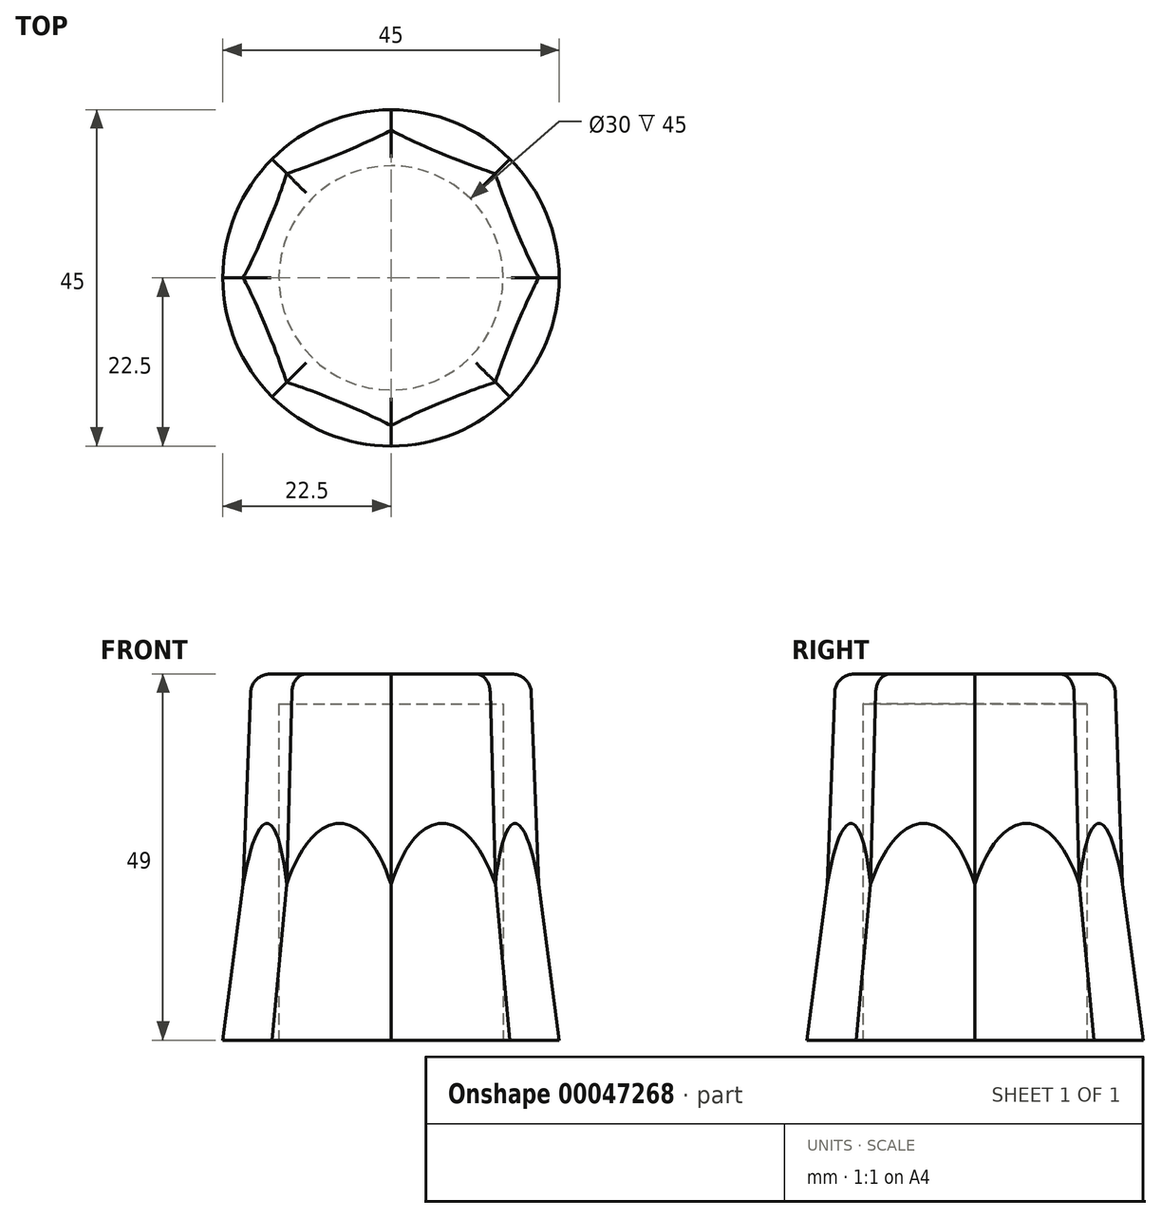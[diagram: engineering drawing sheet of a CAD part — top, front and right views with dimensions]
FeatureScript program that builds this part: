
annotation { "Feature Type Name" : "Feature", "Feature Type Description" : "" }
export const myFeature = defineFeature(function(context is Context, id is Id, definition is map)
    precondition{}
    {
        {
            assignVariable(context, id + "F0", {"name" : "thickness", "anyValue" : 4 * mm});
        }
        {
            var Q0;
            Q0=qCreatedBy(makeId("Top.planeOp"),FACE);
            var sketch = newSketch(context, id + "F1", { "sketchPlane" : qUnion([Q0])});
            skCircle(sketch, "E0.cCircle", {"center": v(0, 0) * mm, "radius": 19 * mm, "construction": true});
            skLineSegment(sketch, "E0.0", {"start": v(-14.54, 14.54) * mm, "end": v(0, 20.57) * mm});
            skLineSegment(sketch, "E0.1", {"start": v(0, 20.57) * mm, "end": v(14.54, 14.54) * mm});
            skLineSegment(sketch, "E0.2", {"start": v(14.54, 14.54) * mm, "end": v(20.57, 0) * mm});
            skLineSegment(sketch, "E0.3", {"start": v(20.57, 0) * mm, "end": v(14.54, -14.54) * mm});
            skLineSegment(sketch, "E0.4", {"start": v(14.54, -14.54) * mm, "end": v(0, -20.57) * mm});
            skLineSegment(sketch, "E0.5", {"start": v(0, -20.57) * mm, "end": v(-14.54, -14.54) * mm});
            skLineSegment(sketch, "E0.6", {"start": v(-14.54, -14.54) * mm, "end": v(-20.57, 0) * mm});
            skLineSegment(sketch, "E0.7", {"start": v(-20.57, 0) * mm, "end": v(-14.54, 14.54) * mm});
            skPoint(sketch, "E0.0.midPoint", {"position": v(-7.27, 17.55) * mm});
            skSolve(sketch);
        }
        {
            var Q0;
            Q0=qCreatedBy(makeId("Top.planeOp"),FACE);
            cPlane(context, id + "F2", {"entities" : qUnion([Q0]), "cplaneType" : CPlaneType.OFFSET, "offset" : 45 * mm + getVariable(context, 'thickness'), "width" : 150 * mm, "height" : 150 * mm});
        }
        {
            var Q0;
            Q0=qCreatedBy(id+"F2.planeOp",FACE);
            var sketch = newSketch(context, id + "F3", { "sketchPlane" : qUnion([Q0])});
            skCircle(sketch, "E1.cCircle", {"center": v(0, 0) * mm, "radius": 17.25 * mm, "construction": true});
            skLineSegment(sketch, "E1.0", {"start": v(-13.2, 13.2) * mm, "end": v(0, 18.67) * mm});
            skLineSegment(sketch, "E1.1", {"start": v(0, 18.67) * mm, "end": v(13.2, 13.2) * mm});
            skLineSegment(sketch, "E1.2", {"start": v(13.2, 13.2) * mm, "end": v(18.67, 0) * mm});
            skLineSegment(sketch, "E1.3", {"start": v(18.67, 0) * mm, "end": v(13.2, -13.2) * mm});
            skLineSegment(sketch, "E1.4", {"start": v(13.2, -13.2) * mm, "end": v(0, -18.67) * mm});
            skLineSegment(sketch, "E1.5", {"start": v(0, -18.67) * mm, "end": v(-13.2, -13.2) * mm});
            skLineSegment(sketch, "E1.6", {"start": v(-13.2, -13.2) * mm, "end": v(-18.67, 0) * mm});
            skLineSegment(sketch, "E1.7", {"start": v(-18.67, 0) * mm, "end": v(-13.2, 13.2) * mm});
            skPoint(sketch, "E1.0.midPoint", {"position": v(-6.6, 15.94) * mm});
            skSolve(sketch);
        }
        {
            var Q0;
            Q0=makeQuery(id+"F1.imprint","IMPRINT",FACE,{"disambiguationData":[TD([[makeQuery(id+"F1.imprint","IMPRINT",EDGE,{"derivedFrom":sQuery(id+"F1.wireOp",EDGE,"E0.0")}),-1.0]])]});
            var Q1;
            Q1=makeQuery(id+"F3.imprint","IMPRINT",FACE,{"disambiguationData":[TD([[makeQuery(id+"F3.imprint","IMPRINT",EDGE,{"derivedFrom":sQuery(id+"F3.wireOp",EDGE,"E1.0")}),-1.0]])]});
            loft(context, id + "F4", {"sheetProfilesArray" : [{ "sheetProfileEntities" : qUnion([Q0]) }, { "sheetProfileEntities" : qUnion([Q1]) }]});
        }
        {
            var Q0;
            Q0=qCreatedBy(makeId("Top.planeOp"),FACE);
            var sketch = newSketch(context, id + "F5", { "sketchPlane" : qUnion([Q0])});
            skCircle(sketch, "E2", {"center": v(0, 0) * mm, "radius": 15 * mm});
            skSolve(sketch);
        }
        {
            var Q0;
            Q0=qCreatedBy(id+"F2.planeOp",FACE);
            cPlane(context, id + "F6", {"entities" : qUnion([Q0]), "cplaneType" : CPlaneType.OFFSET, "offset" : getVariable(context, 'thickness'), "oppositeDirection" : true, "width" : 150 * mm, "height" : 150 * mm});
        }
        {
            var Q0;
            Q0=qCreatedBy(id+"F6.planeOp",FACE);
            var sketch = newSketch(context, id + "F7", { "sketchPlane" : qUnion([Q0])});
            skCircle(sketch, "E3", {"center": v(0, 0) * mm, "radius": 13.25 * mm});
            skSolve(sketch);
        }
        {
            var Q1;
            Q1 = qSketchRegion(id + "F5", true);
            var Q2;
            Q2 = qSketchRegion(id + "F7", true);
            loft(context, id + "F8", {"operationType" : NewBodyOperationType.REMOVE, "sheetProfilesArray" : [{ "sheetProfileEntities" : qUnion([Q1]) }, { "sheetProfileEntities" : qUnion([Q2]) }]});
        }
        {
            var Q0;
            Q0=makeQuery(id+"F4.opLoft","MID_CAP_EDGE",EDGE,{"disambiguationData":[OSD([sQuery(id+"F3.wireOp",EDGE,"E1.5"),sQuery(id+"F3.wireOp",EDGE,"E1.6"),sQuery(id+"F3.wireOp",EDGE,"E1.7")])],"capPos":1.0});
            var Q1;
            Q1=makeQuery(id+"F4.opLoft","MID_CAP_EDGE",EDGE,{"disambiguationData":[OSD([sQuery(id+"F3.wireOp",EDGE,"E1.4"),sQuery(id+"F3.wireOp",EDGE,"E1.5"),sQuery(id+"F3.wireOp",EDGE,"E1.6")])],"capPos":1.0});
            var Q2;
            Q2=makeQuery(id+"F4.opLoft","MID_CAP_EDGE",EDGE,{"disambiguationData":[OSD([sQuery(id+"F3.wireOp",EDGE,"E1.3"),sQuery(id+"F3.wireOp",EDGE,"E1.4"),sQuery(id+"F3.wireOp",EDGE,"E1.5")])],"capPos":1.0});
            var Q3;
            Q3=makeQuery(id+"F4.opLoft","MID_CAP_EDGE",EDGE,{"disambiguationData":[OSD([sQuery(id+"F3.wireOp",EDGE,"E1.2"),sQuery(id+"F3.wireOp",EDGE,"E1.3"),sQuery(id+"F3.wireOp",EDGE,"E1.4")])],"capPos":1.0});
            var Q4;
            Q4=makeQuery(id+"F4.opLoft","MID_CAP_EDGE",EDGE,{"disambiguationData":[OSD([sQuery(id+"F3.wireOp",EDGE,"E1.1"),sQuery(id+"F3.wireOp",EDGE,"E1.2"),sQuery(id+"F3.wireOp",EDGE,"E1.3")])],"capPos":1.0});
            var Q5;
            Q5=makeQuery(id+"F4.opLoft","MID_CAP_EDGE",EDGE,{"disambiguationData":[OSD([sQuery(id+"F3.wireOp",EDGE,"E1.0"),sQuery(id+"F3.wireOp",EDGE,"E1.1"),sQuery(id+"F3.wireOp",EDGE,"E1.2")])],"capPos":1.0});
            var Q6;
            Q6=makeQuery(id+"F4.opLoft","MID_CAP_EDGE",EDGE,{"disambiguationData":[OSD([sQuery(id+"F3.wireOp",EDGE,"E1.0"),sQuery(id+"F3.wireOp",EDGE,"E1.1"),sQuery(id+"F3.wireOp",EDGE,"E1.7")])],"capPos":1.0});
            var Q7;
            Q7=makeQuery(id+"F4.opLoft","MID_CAP_EDGE",EDGE,{"disambiguationData":[OSD([sQuery(id+"F3.wireOp",EDGE,"E1.0"),sQuery(id+"F3.wireOp",EDGE,"E1.6"),sQuery(id+"F3.wireOp",EDGE,"E1.7")])],"capPos":1.0});
            fillet(context, id + "F9", {"entities" : qUnion([Q0, Q1, Q2, Q3, Q4, Q5, Q6, Q7]), "radius" : 2.5 * mm, "tangentPropagation" : true, "allowEdgeOverflow" : false});
        }
        {
            var Q0;
            Q0=qCreatedBy(makeId("Top.planeOp"),FACE);
            var sketch = newSketch(context, id + "F10", { "sketchPlane" : qUnion([Q0])});
            skCircle(sketch, "E4", {"center": v(0, 0) * mm, "radius": 22.5 * mm});
            skSolve(sketch);
        }
        {
            var Q1;
            Q1=makeQuery(id+"F10.imprint","IMPRINT",FACE,{"disambiguationData":[TD([[makeQuery(id+"F10.imprint","IMPRINT",EDGE,{"derivedFrom":sQuery(id+"F10.wireOp",EDGE,"E4")}),1.0]])]});
            var Q2;
            Q2=makeQuery(id+"F4.opLoft","CAP_FACE",FACE,{"disambiguationData":[OSD([makeQuery(id+"F3.imprint","IMPRINT",FACE,{"disambiguationData":[TD([[makeQuery(id+"F3.imprint","IMPRINT",EDGE,{"derivedFrom":sQuery(id+"F3.wireOp",EDGE,"E1.0")}),-1.0]])]})])],"isStart":true});
            loft(context, id + "F11", {"operationType" : NewBodyOperationType.ADD, "sheetProfilesArray" : [{ "sheetProfileEntities" : qUnion([Q1]) }, { "sheetProfileEntities" : qUnion([Q2]) }]});
        }
        {
            var Q0;
            Q0=makeQuery(id+"F11.boolean.opBoolean","MERGE",FACE,{"derivedFrom":[makeQuery(id+"F4.opLoft","CAP_FACE",FACE,{"disambiguationData":[OSD([makeQuery(id+"F1.imprint","IMPRINT",FACE,{"disambiguationData":[TD([[makeQuery(id+"F1.imprint","IMPRINT",EDGE,{"derivedFrom":sQuery(id+"F1.wireOp",EDGE,"E0.0")}),-1.0]])]})])],"isStart":true}),makeQuery(id+"F11.opLoft","CAP_FACE",FACE,{"disambiguationData":[OSD([makeQuery(id+"F10.imprint","IMPRINT",FACE,{"disambiguationData":[TD([[makeQuery(id+"F10.imprint","IMPRINT",EDGE,{"derivedFrom":sQuery(id+"F10.wireOp",EDGE,"E4")}),1.0]])]})])],"isStart":true})]});
            var sketch = newSketch(context, id + "F12", { "sketchPlane" : qUnion([Q0])});
            skCircle(sketch, "E5", {"center": v(0, 0) * mm, "radius": 15 * mm});
            skSolve(sketch);
        }
        {
            var Q0;
            Q0 = qSketchRegion(id + "F12", true);
            extrude(context, id + "F13", {"entities" : qUnion([Q0]), "operationType" : NewBodyOperationType.REMOVE, "oppositeDirection" : true, "depth" : 45 * mm});
        }
    });
